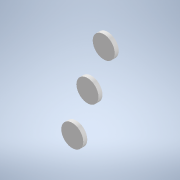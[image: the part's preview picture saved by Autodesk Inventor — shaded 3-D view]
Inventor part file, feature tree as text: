
AUTODESK INVENTOR PART (.ipt)
format: ipt  version: 2020 (Build 240168000, 168)  size: 99,840 bytes
history: native  units: in
note: dims shown in document units (in); Inventor stores cm internally (conversion verified against a paired STEP export)
features: other x10, reference x3, sketch x1, plane x1, extrude x1
ambient origin geometry x8: Origin, YZ Plane, XZ Plane, XY Plane, X Axis, Y Axis, Z Axis, Center Point
bodies: Solid1 (feature_tree)
feature tree (16):
  sketch  "Sketch1"  dims[d0=1.0in d1=0.0in]
  plane  "Work Plane1"
  extrude  "Extrusion1"  [1 undecoded]
  reference  "Reference1"
  reference  "Reference2"
  reference  "Reference3"
  other  "<userpath>\Documents\FRC\2020\Prototype1.iam"
  other  "Prototype1.iam"
  other  "DriveBase2020:1"
  other  "AM14U3 Long Half:2"
  other  "6 HiGrip with bearings, pulleys and spacers_5"
  other  "6 HiGrip Asm Rev II_65"
  other  "6 wheel tread II_2"
  other  "6 HiGrip with hub and double pulley_6"
  other  "6 HiGrip Asm Rev II_46"
  other  "6 HiGrip with bearings, pulleys and spacers_4"
note: 1 required parameter value undecoded (feature->parameter linkage not recoverable at this tier; creation-order binding heuristic only, values carry confidence <= 0.55)
